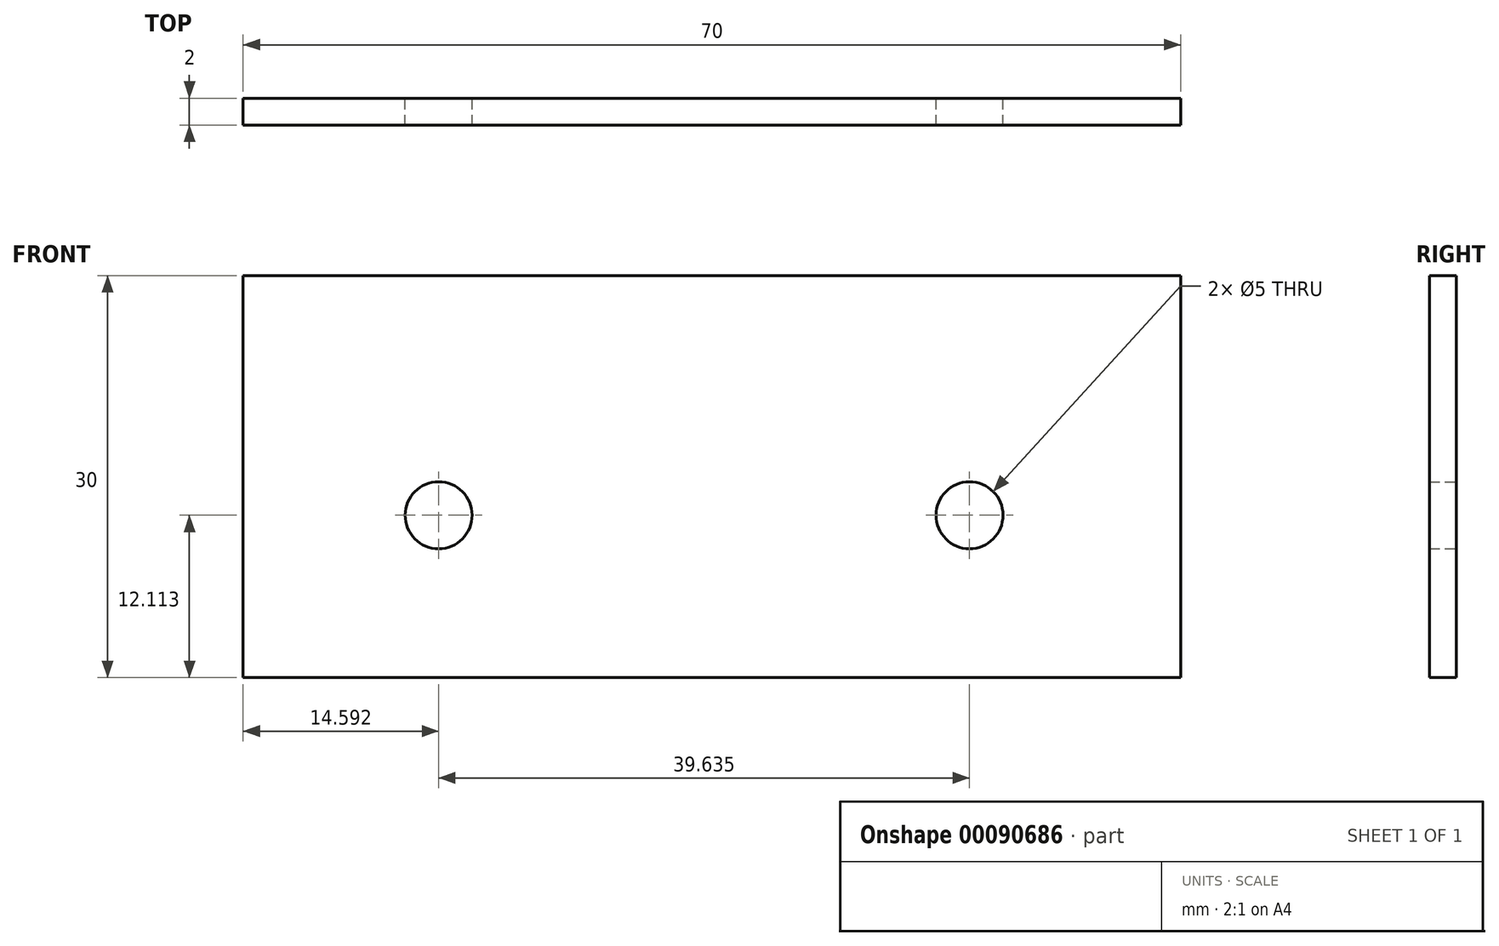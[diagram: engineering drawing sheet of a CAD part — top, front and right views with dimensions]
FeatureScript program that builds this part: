
annotation { "Feature Type Name" : "Feature", "Feature Type Description" : "" }
export const myFeature = defineFeature(function(context is Context, id is Id, definition is map)
    precondition{}
    {
        {
            var Q0;
            Q0=qCreatedBy(makeId("Front.planeOp"),FACE);
            var sketch = newSketch(context, id + "F0", { "sketchPlane" : qUnion([Q0])});
            skLineSegment(sketch, "E0.bottom", {"start": v(-34.4, -0.6) * mm, "end": v(35.6, -0.6) * mm});
            skLineSegment(sketch, "E0.top", {"start": v(-34.4, -30.6) * mm, "end": v(35.6, -30.6) * mm});
            skLineSegment(sketch, "E0.left", {"start": v(-34.4, -0.6) * mm, "end": v(-34.4, -30.6) * mm});
            skLineSegment(sketch, "E0.right", {"start": v(35.6, -0.6) * mm, "end": v(35.6, -30.6) * mm});
            skCircle(sketch, "E1", {"center": v(-19.82, -18.49) * mm, "radius": 2.5 * mm});
            skCircle(sketch, "E2.MirrorC", {"center": v(19.82, -18.49) * mm, "radius": 2.5 * mm});
            skSolve(sketch);
        }
        {
            var Q0;
            Q0=makeQuery(id+"F0.imprint","IMPRINT",FACE,{"disambiguationData":[TD([[makeQuery(id+"F0.imprint","IMPRINT",EDGE,{"derivedFrom":sQuery(id+"F0.wireOp",EDGE,"E0.bottom")}),-1.0]])]});
            extrude(context, id + "F1", {"entities" : qUnion([Q0]), "depth" : 2 * mm});
        }
    });
